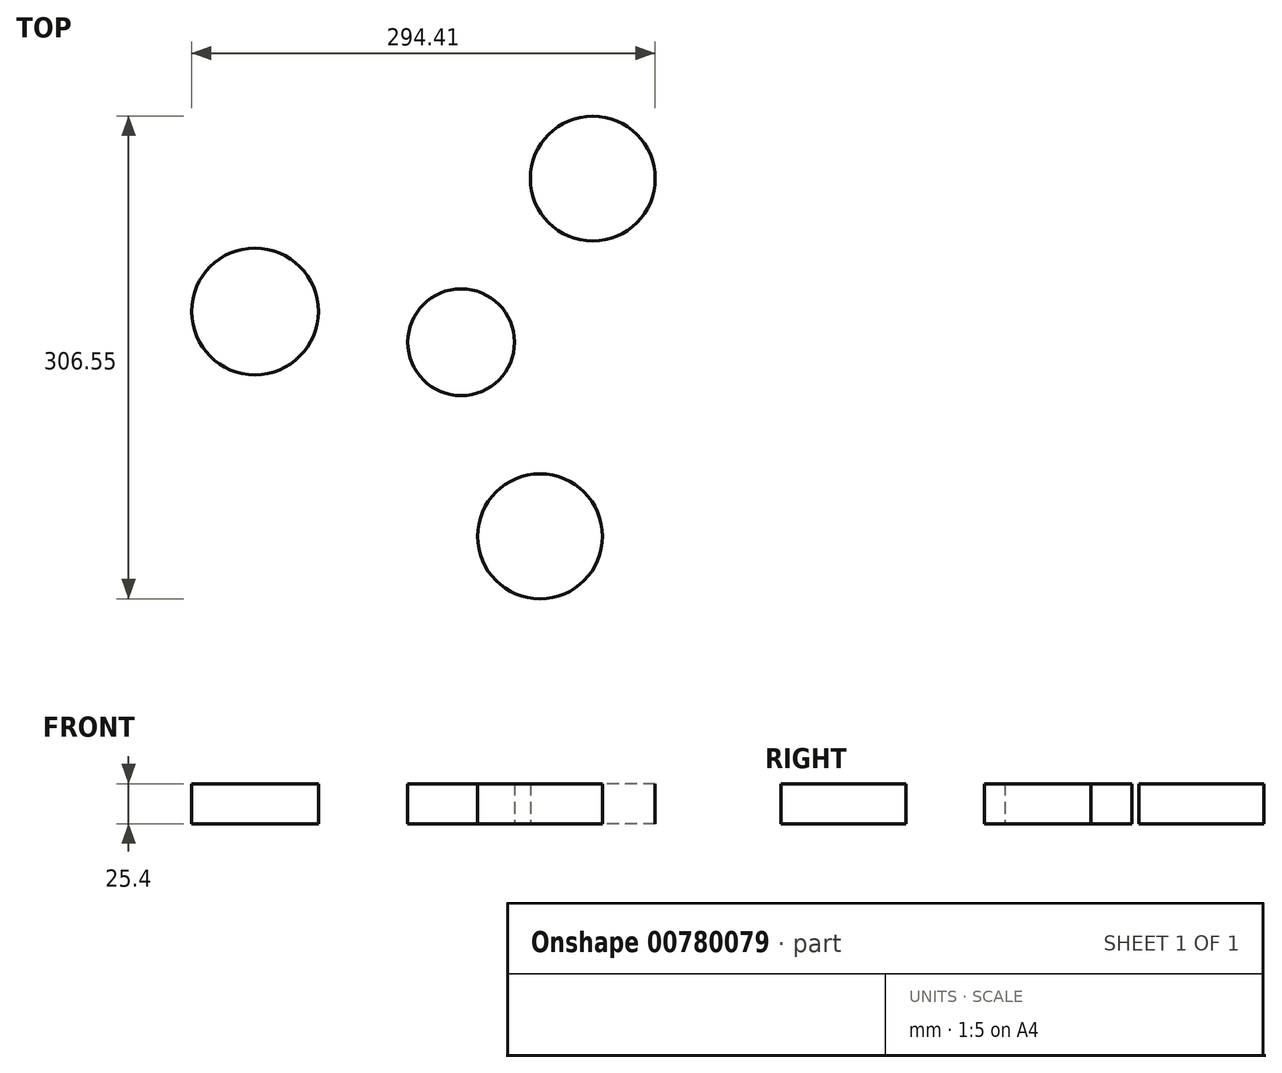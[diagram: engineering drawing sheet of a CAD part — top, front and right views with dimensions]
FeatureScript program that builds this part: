
annotation { "Feature Type Name" : "Feature", "Feature Type Description" : "" }
export const myFeature = defineFeature(function(context is Context, id is Id, definition is map)
    precondition{}
    {
        {
            var Q0;
            Q0=qCreatedBy(makeId("Top.planeOp"),FACE);
            var sketch = newSketch(context, id + "F0", { "sketchPlane" : qUnion([Q0])});
            skCircle(sketch, "E0.1.0", {"center": v(49.39, -123.78) * mm, "radius": 33.3 * mm});
            skCircle(sketch, "E0.2.0", {"center": v(82.85, 103.46) * mm, "radius": 33.3 * mm});
            skPoint(sketch, "E0.center", {"position": v(0.52, -0.5) * mm});
            skPoint(sketch, "E1.center", {"position": v(0, 0) * mm});
            skCircle(sketch, "E2", {"center": v(-131.65, 19.08) * mm, "radius": 33.9 * mm});
            skCircle(sketch, "E3", {"center": v(-0.75, -0.5) * mm, "radius": 33.9 * mm});
            skCircle(sketch, "E4.0", {"center": v(49.39, -123.78) * mm, "radius": 39.65 * mm});
            skCircle(sketch, "E5.0", {"center": v(-131.65, 19.08) * mm, "radius": 40.25 * mm});
            skArc(sketch, "E6", {"start": v(10.19, -117.8) * mm, "mid": v(-42.96, -43.4) * mm, "end": v(-131.65, -21.17) * mm});
            skArc(sketch, "E7.1.0", {"start": v(96.92, 67.72) * mm, "mid": v(59.06, -15.5) * mm, "end": v(84.16, -103.43) * mm});
            skArc(sketch, "E7.2.0", {"start": v(-107.1, 50.08) * mm, "mid": v(-16.1, 58.9) * mm, "end": v(47.5, 124.6) * mm});
            skCircle(sketch, "E8.0", {"center": v(82.85, 103.46) * mm, "radius": 39.65 * mm});
            skSolve(sketch);
        }
        {
            var Q0;
            Q0=makeQuery(id+"F0.imprint","IMPRINT",FACE,{"disambiguationData":[TD([[makeQuery(id+"F0.imprint","IMPRINT",EDGE,{"derivedFrom":sQuery(id+"F0.wireOp",EDGE,"E3")}),1.0]])]});
            var Q1;
            Q1=makeQuery(id+"F0.imprint","IMPRINT",FACE,{"disambiguationData":[TD([[makeQuery(id+"F0.imprint","IMPRINT",EDGE,{"derivedFrom":sQuery(id+"F0.wireOp",EDGE,"E2")}),1.0]])]});
            var Q2;
            Q2=makeQuery(id+"F0.imprint","IMPRINT",FACE,{"disambiguationData":[TD([[makeQuery(id+"F0.imprint","IMPRINT",EDGE,{"derivedFrom":sQuery(id+"F0.wireOp",EDGE,"E2")}),-1.0]])]});
            var Q3;
            Q3=makeQuery(id+"F0.imprint","IMPRINT",FACE,{"disambiguationData":[TD([[makeQuery(id+"F0.imprint","IMPRINT",EDGE,{"derivedFrom":sQuery(id+"F0.wireOp",EDGE,"E0.1.0")}),1.0]])]});
            var Q4;
            Q4=makeQuery(id+"F0.imprint","IMPRINT",FACE,{"disambiguationData":[TD([[makeQuery(id+"F0.imprint","IMPRINT",EDGE,{"derivedFrom":sQuery(id+"F0.wireOp",EDGE,"E0.2.0")}),-1.0]])]});
            var Q5;
            Q5=makeQuery(id+"F0.imprint","IMPRINT",FACE,{"disambiguationData":[TD([[makeQuery(id+"F0.imprint","IMPRINT",EDGE,{"derivedFrom":sQuery(id+"F0.wireOp",EDGE,"E0.1.0")}),-1.0]])]});
            var Q6;
            Q6=makeQuery(id+"F0.imprint","IMPRINT",FACE,{"disambiguationData":[TD([[makeQuery(id+"F0.imprint","IMPRINT",EDGE,{"derivedFrom":sQuery(id+"F0.wireOp",EDGE,"E0.2.0")}),1.0]])]});
            var Q7;
            {var subQ0=sQuery(id+"F0.wireOp",EDGE,"E5.0");var subQ1=sQuery(id+"F0.wireOp",EDGE,"E6");var subQ2=makeQuery(id+"F0.imprint","INTERSECT",VERTEX,{"disambiguationData":[OD(0.0)],"derivedFrom":[subQ1,subQ0]});Q7=makeQuery(id+"F0.imprint","IMPRINT",FACE,{"disambiguationData":[TD([[makeQuery(id+"F0.imprint","IMPRINT",EDGE,{"disambiguationData":[TD([[subQ2,1.0]])],"derivedFrom":subQ1}),1.0]])]});}
            extrude(context, id + "F1", {"entities" : qUnion([Q0, Q1, Q2, Q3, Q4, Q5, Q6, Q7]), "depth" : 25.4 * mm, "offsetDistance" : 25.4 * mm});
        }
    });
